# Revit family: Клапан воздушный с эл.приводом VR1_VEOX
name_source: partatom
category: Арматура воздуховодов
units: mm (PartAtom-declared; Revit-internal decimal feet)

## family parameters
Всегда вертикально = Нет
На основе рабочей плоскости = Нет
Общий = Нет
При загрузке вырезать с полостями = Нет
Размер круглого соединителя = Использовать диаметр
Тип детали = Вставляется

## types (4) — shared parameters
A = 200 мм
ADSK_Версия Revit = 2019
ADSK_Версия семейства = 2025.01.18
ADSK_Единица измерения = шт.
ADSK_Завод-изготовитель = VEOX
ADSK_Количество = 1
ADSK_Наименование краткое = Заслонка воздушная
ADSK_Обозначение = VR1
B = 100 мм
Bh = 10 мм
Data = ДК D
Описание = Заслонка воздушная
zero-valued in all types: ADSK_Материал тип подсчета

## per-type parameters (varying)
| type | K1 | тип |
| аналоговый, 24 В, оцинкованный | 6 | 1 |
| трехпозиционный, 24 В, оцинкованный | 6 | 11 |
| аналоговый, 24 В, нержавеющая сталь | 6 | 2 |
| трехпозиционный, 24 В, нержавеющая сталь | 5.2 | 22 |

## geometry (parser evidence)
native form markers: Blend x4
no freeform markers — native parametric forms only
